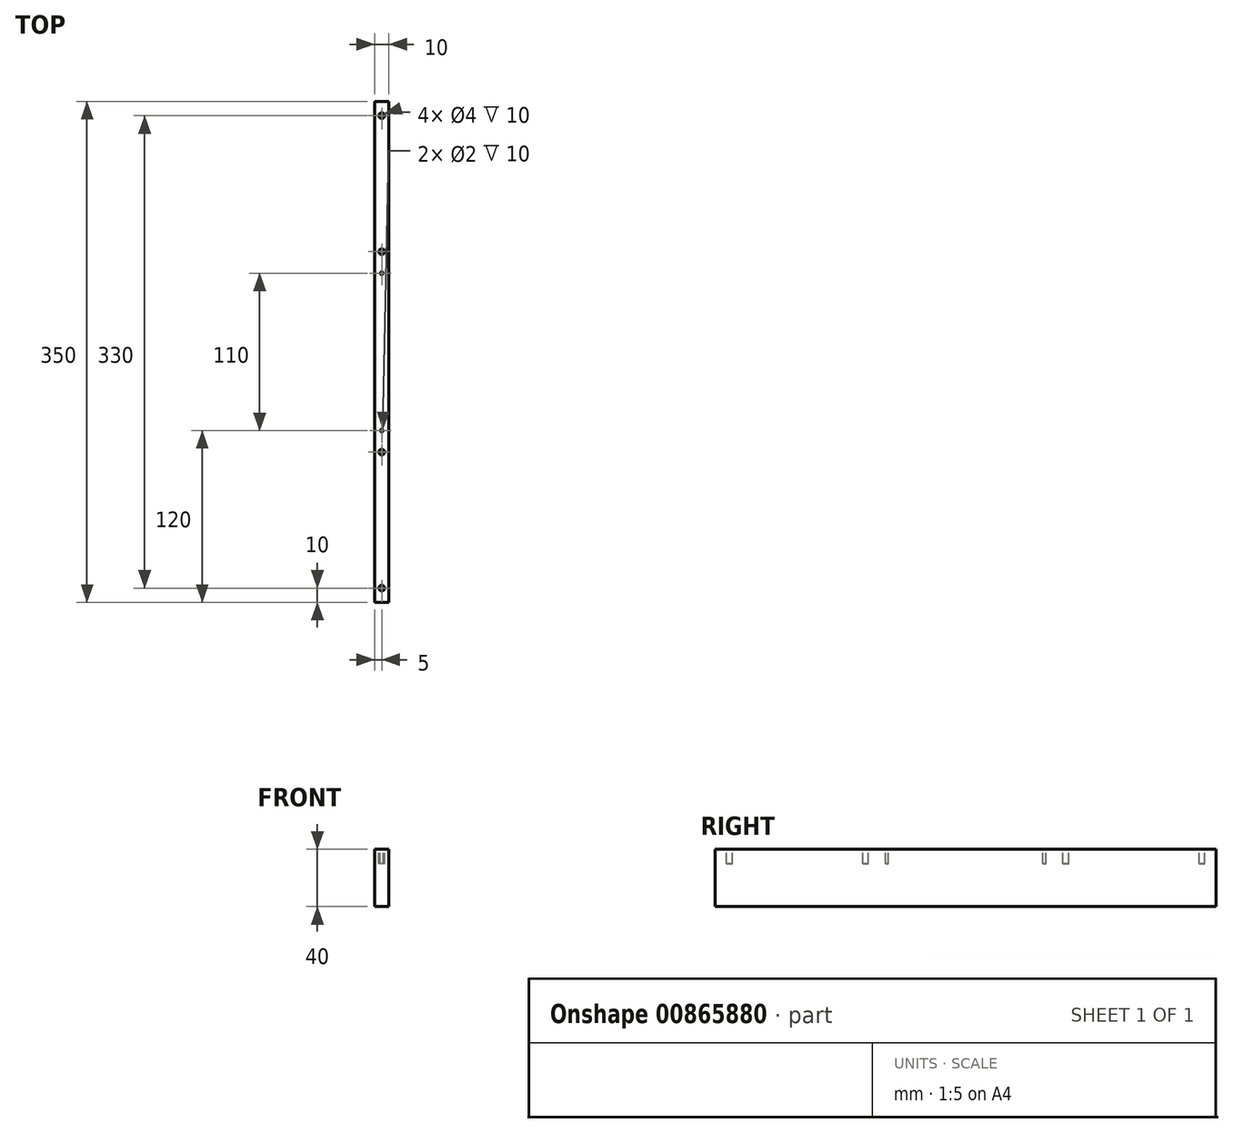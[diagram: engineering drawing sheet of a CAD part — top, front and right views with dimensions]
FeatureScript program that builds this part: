
annotation { "Feature Type Name" : "Feature", "Feature Type Description" : "" }
export const myFeature = defineFeature(function(context is Context, id is Id, definition is map)
    precondition{}
    {
        {
            var Q0;
            Q0=qCreatedBy(makeId("Front.planeOp"),FACE);
            var sketch = newSketch(context, id + "F0", { "sketchPlane" : qUnion([Q0])});
            skLineSegment(sketch, "E0.bottom", {"start": v(0, 0) * mm, "end": v(10, 0) * mm});
            skLineSegment(sketch, "E0.top", {"start": v(0, 40) * mm, "end": v(10, 40) * mm});
            skLineSegment(sketch, "E0.left", {"start": v(0, 0) * mm, "end": v(0, 40) * mm});
            skLineSegment(sketch, "E0.right", {"start": v(10, 0) * mm, "end": v(10, 40) * mm});
            skSolve(sketch);
        }
        {
            var Q0;
            Q0 = qSketchRegion(id + "F0", true);
            extrude(context, id + "F1", {"entities" : qUnion([Q0]), "depth" : 350 * mm, "offsetDistance" : 25 * mm});
        }
        {
            var Q0;
            Q0=makeQuery(id+"F1.opExtrude","SWEPT_FACE",FACE,{"disambiguationData":[OSD([sQuery(id+"F0.wireOp",EDGE,"E0.top")])]});
            var sketch = newSketch(context, id + "F2", { "sketchPlane" : qUnion([Q0])});
            skCircle(sketch, "E1", {"center": v(5, -120) * mm, "radius": 1 * mm});
            skCircle(sketch, "E2", {"center": v(5, -230) * mm, "radius": 1 * mm});
            skCircle(sketch, "E3", {"center": v(5, -340) * mm, "radius": 2 * mm});
            skPoint(sketch, "E3.centerSnap0", {"position": v(5, -350) * mm});
            skCircle(sketch, "E4", {"center": v(5, -245) * mm, "radius": 2 * mm});
            skCircle(sketch, "E5", {"center": v(5, -10) * mm, "radius": 2 * mm});
            skPoint(sketch, "E5.centerSnap0", {"position": v(5, 0) * mm});
            skCircle(sketch, "E6", {"center": v(5, -105) * mm, "radius": 2 * mm});
            skSolve(sketch);
        }
        {
            var Q0;
            Q0 = qSketchRegion(id + "F2", true);
            extrude(context, id + "F3", {"entities" : qUnion([Q0]), "operationType" : NewBodyOperationType.REMOVE, "oppositeDirection" : true, "depth" : 10 * mm, "offsetDistance" : 25 * mm});
        }
    });
